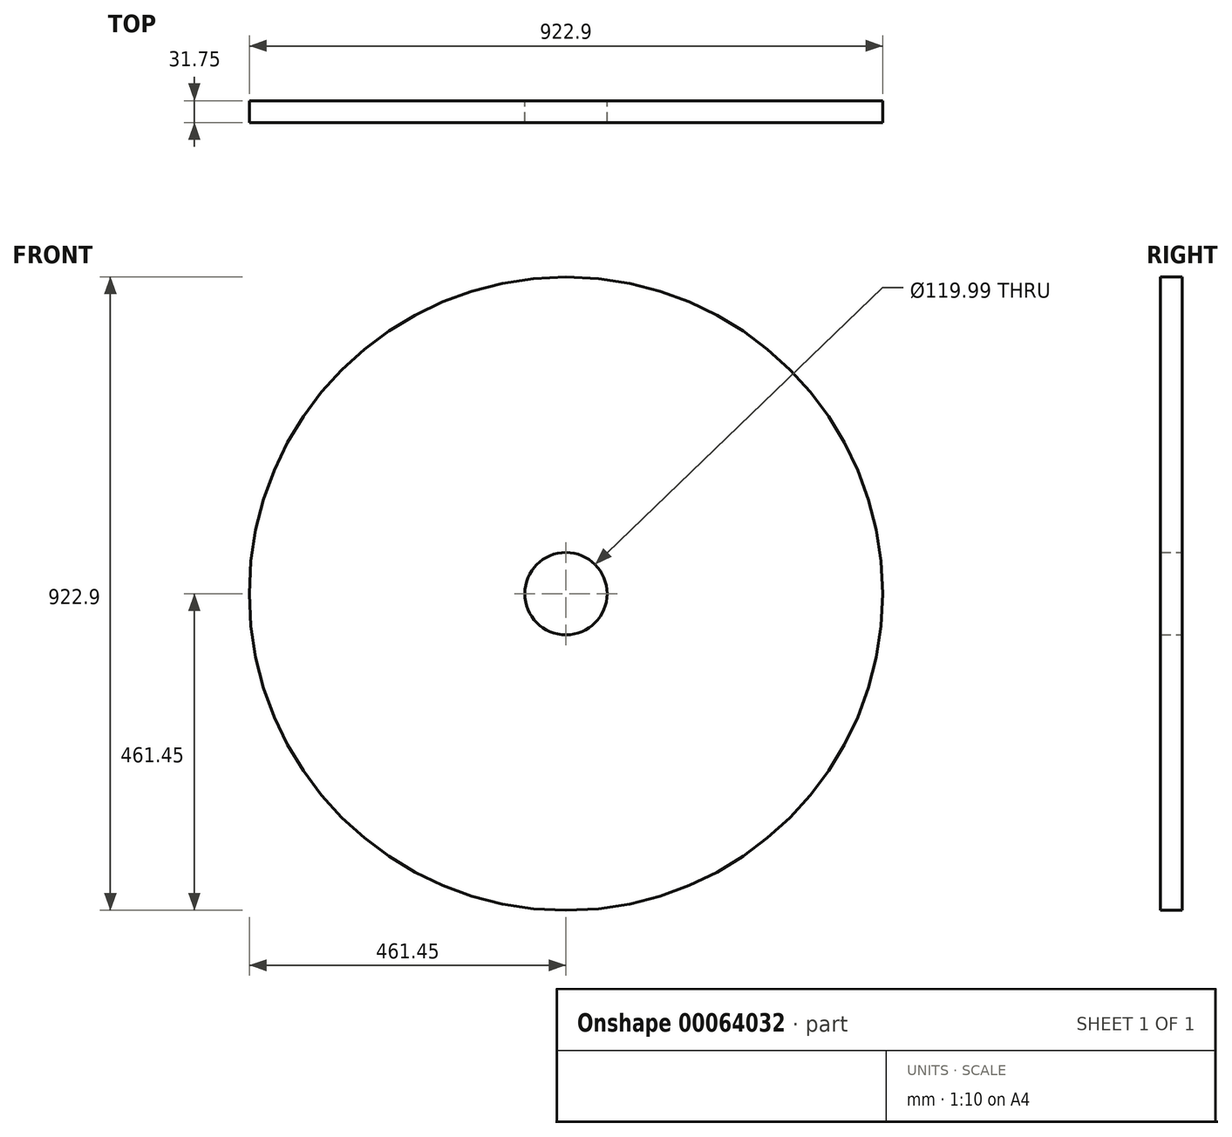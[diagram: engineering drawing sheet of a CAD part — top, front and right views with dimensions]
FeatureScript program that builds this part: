
annotation { "Feature Type Name" : "Feature", "Feature Type Description" : "" }
export const myFeature = defineFeature(function(context is Context, id is Id, definition is map)
    precondition{}
    {
        {
            var Q0;
            Q0=qCreatedBy(makeId("Front.planeOp"),FACE);
            var sketch = newSketch(context, id + "F0", { "sketchPlane" : qUnion([Q0])});
            skCircle(sketch, "E0", {"center": v(0, 0) * mm, "radius": 461.45 * mm});
            skCircle(sketch, "E1", {"center": v(0, 0) * mm, "radius": 60 * mm});
            skSolve(sketch);
        }
        {
            var Q0;
            Q0=makeQuery(id+"F0.imprint","IMPRINT",FACE,{"disambiguationData":[TD([[makeQuery(id+"F0.imprint","IMPRINT",EDGE,{"derivedFrom":sQuery(id+"F0.wireOp",EDGE,"E0")}),1.0]])]});
            extrude(context, id + "F1", {"entities" : qUnion([Q0]), "depth" : 31.75 * mm});
        }
    });
